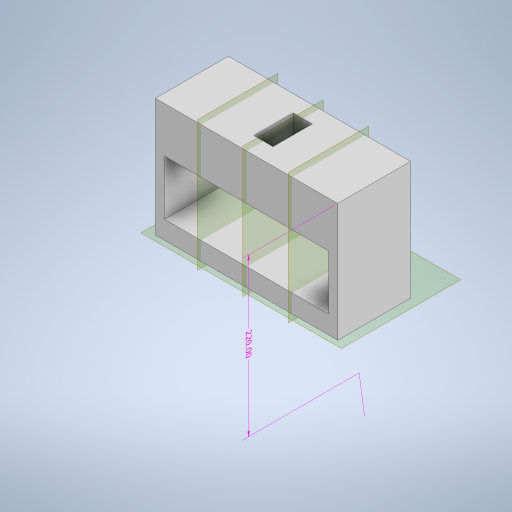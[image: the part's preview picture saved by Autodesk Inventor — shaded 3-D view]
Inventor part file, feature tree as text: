
AUTODESK INVENTOR PART (.ipt)
format: ipt  version: 2023 (Build 270158000, 158)  size: 320,512 bytes
history: native  units: mm
features: extrude x6, plane x6, sketch x6, other x5, split x1
ambient origin geometry x8: Origin, YZ Plane, XZ Plane, XY Plane, X Axis, Y Axis, Z Axis, Center Point
bodies: Body1 (feature_tree), Body2 (feature_tree)
feature tree (24):
  other  "Sólido1"
  other  "Anotaciones"
  extrude  "Extrusión1"  Depth=80.0mm
  extrude  "Extrusión2"  Depth=180.0mm
  extrude  "Extrusión3"  Depth=20.0mm
  extrude  "Extrusión4"  Depth=21.0mm
  plane  "Plano de trabajo1"
  extrude  "Extrusión6"  Depth=20.0mm
  plane  "Plano de trabajo3"
  extrude  "Extrusión7"  [1 undecoded]
  plane  "Plano de trabajo4"
  split  "Dividir1"
  other  "Suprimir cara4"
  plane  "Plano de trabajo5"
  plane  "Plano de trabajo6"
  plane  "Plano de trabajo7"
  sketch  "Boceto1"  dims[d0=200.0mm d1=80.0mm]
  sketch  "Boceto2"  dims[d2=130.0mm d3=0.0mm d4=180.0mm]
  sketch  "Boceto3"  dims[d5=60.0mm d6=20.0mm]
  sketch  "Boceto4"  dims[d7=60.0mm d8=0.0mm d9=21.0mm d10=43.0mm]
  sketch  "Boceto7"  dims[d11=43.0mm d12=0.0mm d13=20.0mm]
  other  "Sólido3"
  sketch  "Boceto10"  dims[d14=90.0mm d15=0.0mm d16=-90.0mm d28=20.0mm d29=20.0mm d30=30.0mm d31=30.0mm d32=20.0mm d33=35.0mm d34=35.0mm d35=69.0mm d36=10.0mm d37=0.0mm d45=1.5mm d50=10.0mm d51=0.0mm d52=10.0mm d53=89.5mm d54=90.0deg d38=3.166395mm d39=4.283575mm d40=220.0mm]
  other  "Cota lineal 1"
note: 1 required parameter value undecoded (feature->parameter linkage not recoverable at this tier; creation-order binding heuristic only, values carry confidence <= 0.55)
